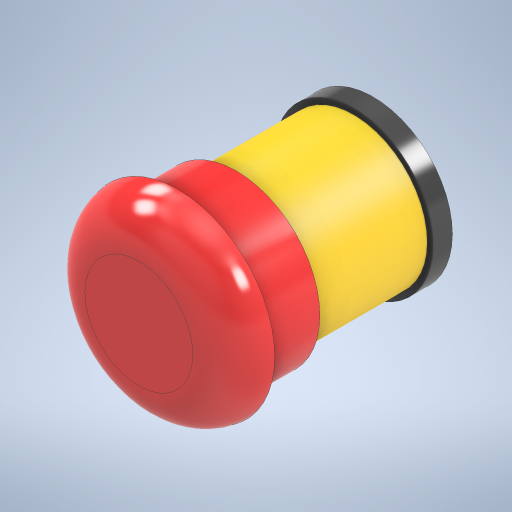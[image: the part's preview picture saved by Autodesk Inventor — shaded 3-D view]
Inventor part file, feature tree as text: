
AUTODESK INVENTOR PART (.ipt)
format: ipt  version: 2023 (Build 270158000, 158)  size: 326,656 bytes
history: native  units: in
note: dims shown in document units (in); Inventor stores cm internally (conversion verified against a paired STEP export)
features: extrude x4, sketch x4, fillet x1
ambient origin geometry x8: Origin, YZ Plane, XZ Plane, XY Plane, X Axis, Y Axis, Z Axis, Center Point
bodies: Solid1 (feature_tree)
feature tree (9):
  extrude  "Extrusion1"  Depth=0.1969in TaperAngle=0.0deg
  extrude  "Extrusion4"  Depth=0.5906in TaperAngle=0.0deg
  extrude  "Extrusion5"  Depth=0.4331in
  extrude  "Extrusion6"  [1 undecoded]
  fillet  "Fillet1"  [1 undecoded]
  sketch  "Sketch1"  dims[d0=1.6in d1=0.1969in d2=0.0in]
  sketch  "Sketch2"  dims[d7=1.1811in d8=0.0in d9=0.5906in d10=0.0in]
  sketch  "Sketch3"  dims[d11=0.3937in d12=0.0in d13=0.4331in]
  sketch  "Sketch4"
note: 2 required parameter values undecoded (feature->parameter linkage not recoverable at this tier; creation-order binding heuristic only, values carry confidence <= 0.55)
